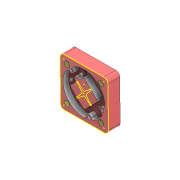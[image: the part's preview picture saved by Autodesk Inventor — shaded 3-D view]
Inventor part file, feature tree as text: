
AUTODESK INVENTOR PART (.ipt)
format: ipt  version: 2022 (Build 260153000, 153)  size: 1,039,360 bytes
history: native  units: mm
features: projected_geometry x17, sketch x7, other x5, hole x3, extrude x3, reference x2
ambient origin geometry x8: Origin, YZ Plane, XZ Plane, XY Plane, X Axis, Y Axis, Z Axis, Center Point
bodies: Volumenkörper1 (feature_tree)
feature tree (37):
  other  "IM_Mold_plate.ipt"
  sketch  "Skizze1"  dims[d0=10.0mm]
  hole  "Bohrung1"  [1 undecoded]
  extrude  "Extrusion1"  Depth=8.0mm
  hole  "Bohrung2"  [1 undecoded]
  hole  "Bohrung3"  [1 undecoded]
  extrude  "Extrusion2"  [1 undecoded]
  extrude  "Extrusion3"  [1 undecoded]
  other  "Volumenkörper5::IM_Mold_plate.ipt"
  other  "Bezeichnung1"
  reference  "Referenz1"
  sketch  "Skizze2"  dims[d1=6.0mm d2=6.0mm d3=8.0mm d4=1.0mm d5=90.0deg d6=8.0mm d7=20.594885mm d8=1.0mm d9=0.0mm]
  reference  "Referenz2"
  projected_geometry  "Projizierte Kontur1"
  sketch  "Skizze3"  dims[d10=3.2mm d11=6.0mm d12=6.5mm d13=3.0mm d14=90.0deg d15=8.0mm d16=20.594885mm]
  projected_geometry  "Projizierte Kontur2"
  sketch  "Skizze4"  dims[d17=3.7mm d18=6.0mm d19=6.5mm d20=3.0mm d21=90.0deg d22=8.0mm d23=20.594885mm d24=8.0mm d25=0.174533mm]
  projected_geometry  "Projizierte Kontur3"
  sketch  "Skizze5"  dims[d26=16.015316mm d27=10.0mm d28=0.0mm]
  projected_geometry  "Projizierte Kontur4"
  sketch  "Skizze6"
  projected_geometry  "Projizierte Kontur5"
  projected_geometry  "Projizierte Kontur6"
  projected_geometry  "Projizierte Kontur7"
  projected_geometry  "Projizierte Kontur8"
  projected_geometry  "Projizierte Kontur9"
  projected_geometry  "Projizierte Kontur10"
  projected_geometry  "Projizierte Kontur11"
  projected_geometry  "Projizierte Kontur12"
  projected_geometry  "Projizierte Kontur13"
  projected_geometry  "Projizierte Kontur14"
  sketch  "Skizze7"
  projected_geometry  "Projizierte Kontur15"
  projected_geometry  "Projizierte Kontur16"
  projected_geometry  "Projizierte Kontur17"
  other  "IM_Mold_plate_top.ipt.iam"
  other  "IM_Mold_plate:1"
note: 5 required parameter values undecoded (feature->parameter linkage not recoverable at this tier; creation-order binding heuristic only, values carry confidence <= 0.55)
